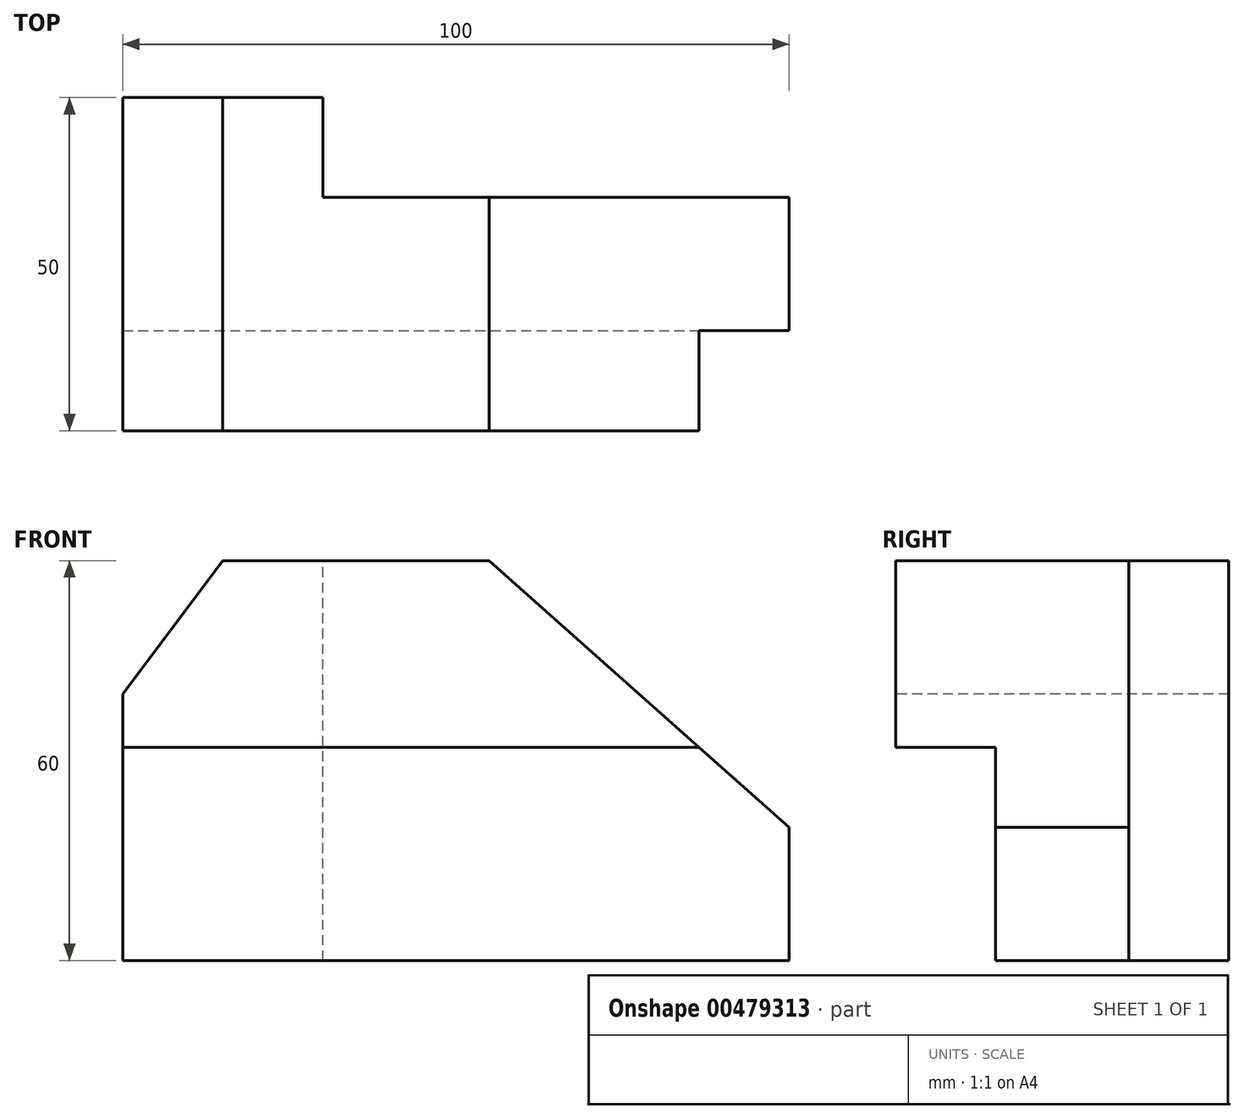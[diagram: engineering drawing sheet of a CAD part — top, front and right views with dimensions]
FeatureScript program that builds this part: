
annotation { "Feature Type Name" : "Feature", "Feature Type Description" : "" }
export const myFeature = defineFeature(function(context is Context, id is Id, definition is map)
    precondition{}
    {
        {
            var Q0;
            Q0=qCreatedBy(makeId("Top.planeOp"),FACE);
            var sketch = newSketch(context, id + "F0", { "sketchPlane" : qUnion([Q0])});
            skLineSegment(sketch, "E0.bottom", {"start": v(0, 0) * mm, "end": v(100, 0) * mm});
            skLineSegment(sketch, "E0.top", {"start": v(0, 50) * mm, "end": v(100, 50) * mm});
            skLineSegment(sketch, "E0.left", {"start": v(0, 0) * mm, "end": v(0, 50) * mm});
            skLineSegment(sketch, "E0.right", {"start": v(100, 0) * mm, "end": v(100, 50) * mm});
            skSolve(sketch);
        }
        {
            var Q0;
            Q0 = qSketchRegion(id + "F0", true);
            extrude(context, id + "F1", {"entities" : qUnion([Q0]), "depth" : 60 * mm});
        }
        {
            var Q0;
            Q0=makeQuery(id+"F1.opExtrude","CAP_FACE",FACE,{"disambiguationData":[OSD([sQuery(id+"F0.wireOp",EDGE,"E0.bottom"),sQuery(id+"F0.wireOp",EDGE,"E0.top"),sQuery(id+"F0.wireOp",EDGE,"E0.left"),sQuery(id+"F0.wireOp",EDGE,"E0.right")])],"isStart":false});
            var sketch = newSketch(context, id + "F2", { "sketchPlane" : qUnion([Q0])});
            skLineSegment(sketch, "E1.bottom", {"start": v(100, 50) * mm, "end": v(30, 50) * mm});
            skLineSegment(sketch, "E1.top", {"start": v(100, 35) * mm, "end": v(30, 35) * mm});
            skLineSegment(sketch, "E1.left", {"start": v(100, 50) * mm, "end": v(100, 35) * mm});
            skLineSegment(sketch, "E1.right", {"start": v(30, 50) * mm, "end": v(30, 35) * mm});
            skSolve(sketch);
        }
        {
            var Q0;
            Q0=makeQuery(id+"F1.opExtrude","SWEPT_FACE",FACE,{"disambiguationData":[OSD([sQuery(id+"F0.wireOp",EDGE,"E0.bottom")])]});
            var sketch = newSketch(context, id + "F3", { "sketchPlane" : qUnion([Q0])});
            skLineSegment(sketch, "E2", {"start": v(100, 20) * mm, "end": v(55, 60) * mm});
            skSolve(sketch);
        }
        {
            var Q0;
            {var subQ0=sQuery(id+"F3.wireOp",EDGE,"E2");Q0=makeQuery(id+"F3.imprint","IMPRINT",FACE,{"disambiguationData":[TD([[makeQuery(id+"F3.imprint","IMPRINT",EDGE,{"derivedFrom":subQ0}),-1.0]])]});}
            extrude(context, id + "F4", {"entities" : qUnion([Q0]), "operationType" : NewBodyOperationType.REMOVE, "endBound" : BoundingType.THROUGH_ALL, "oppositeDirection" : true, "depth" : 25 * mm});
        }
        {
            var Q0;
            Q0 = qSketchRegion(id + "F2", true);
            extrude(context, id + "F5", {"entities" : qUnion([Q0]), "operationType" : NewBodyOperationType.REMOVE, "endBound" : BoundingType.THROUGH_ALL, "oppositeDirection" : true, "depth" : 25 * mm});
        }
        {
            var Q0;
            Q0=makeQuery(id+"F1.opExtrude","SWEPT_FACE",FACE,{"disambiguationData":[OSD([sQuery(id+"F0.wireOp",EDGE,"E0.right")])]});
            var sketch = newSketch(context, id + "F6", { "sketchPlane" : qUnion([Q0])});
            skLineSegment(sketch, "E3.bottom", {"start": v(0, 0) * mm, "end": v(15, 0) * mm});
            skLineSegment(sketch, "E3.top", {"start": v(0, 32) * mm, "end": v(15, 32) * mm});
            skLineSegment(sketch, "E3.left", {"start": v(0, 0) * mm, "end": v(0, 32) * mm});
            skLineSegment(sketch, "E3.right", {"start": v(15, 0) * mm, "end": v(15, 32) * mm});
            skSolve(sketch);
        }
        {
            var Q0;
            Q0 = qSketchRegion(id + "F6", true);
            extrude(context, id + "F7", {"entities" : qUnion([Q0]), "operationType" : NewBodyOperationType.REMOVE, "endBound" : BoundingType.THROUGH_ALL, "oppositeDirection" : true, "depth" : 25 * mm});
        }
        {
            var Q0;
            Q0=makeQuery(id+"F1.opExtrude","SWEPT_FACE",FACE,{"disambiguationData":[OSD([sQuery(id+"F0.wireOp",EDGE,"E0.bottom")])]});
            var sketch = newSketch(context, id + "F8", { "sketchPlane" : qUnion([Q0])});
            skLineSegment(sketch, "E4", {"start": v(15, 60) * mm, "end": v(0, 40) * mm});
            skSolve(sketch);
        }
        {
            var Q0;
            Q0 = qSketchRegion(id + "F8", true);
            var Q1;
            {var subQ0=sQuery(id+"F8.wireOp",EDGE,"E4");Q1=makeQuery(id+"F8.imprint","IMPRINT",FACE,{"disambiguationData":[TD([[makeQuery(id+"F8.imprint","IMPRINT",EDGE,{"derivedFrom":subQ0}),-1.0]])]});}
            extrude(context, id + "F9", {"entities" : qUnion([Q0, Q1]), "operationType" : NewBodyOperationType.REMOVE, "endBound" : BoundingType.THROUGH_ALL, "oppositeDirection" : true, "depth" : 25 * mm});
        }
    });
